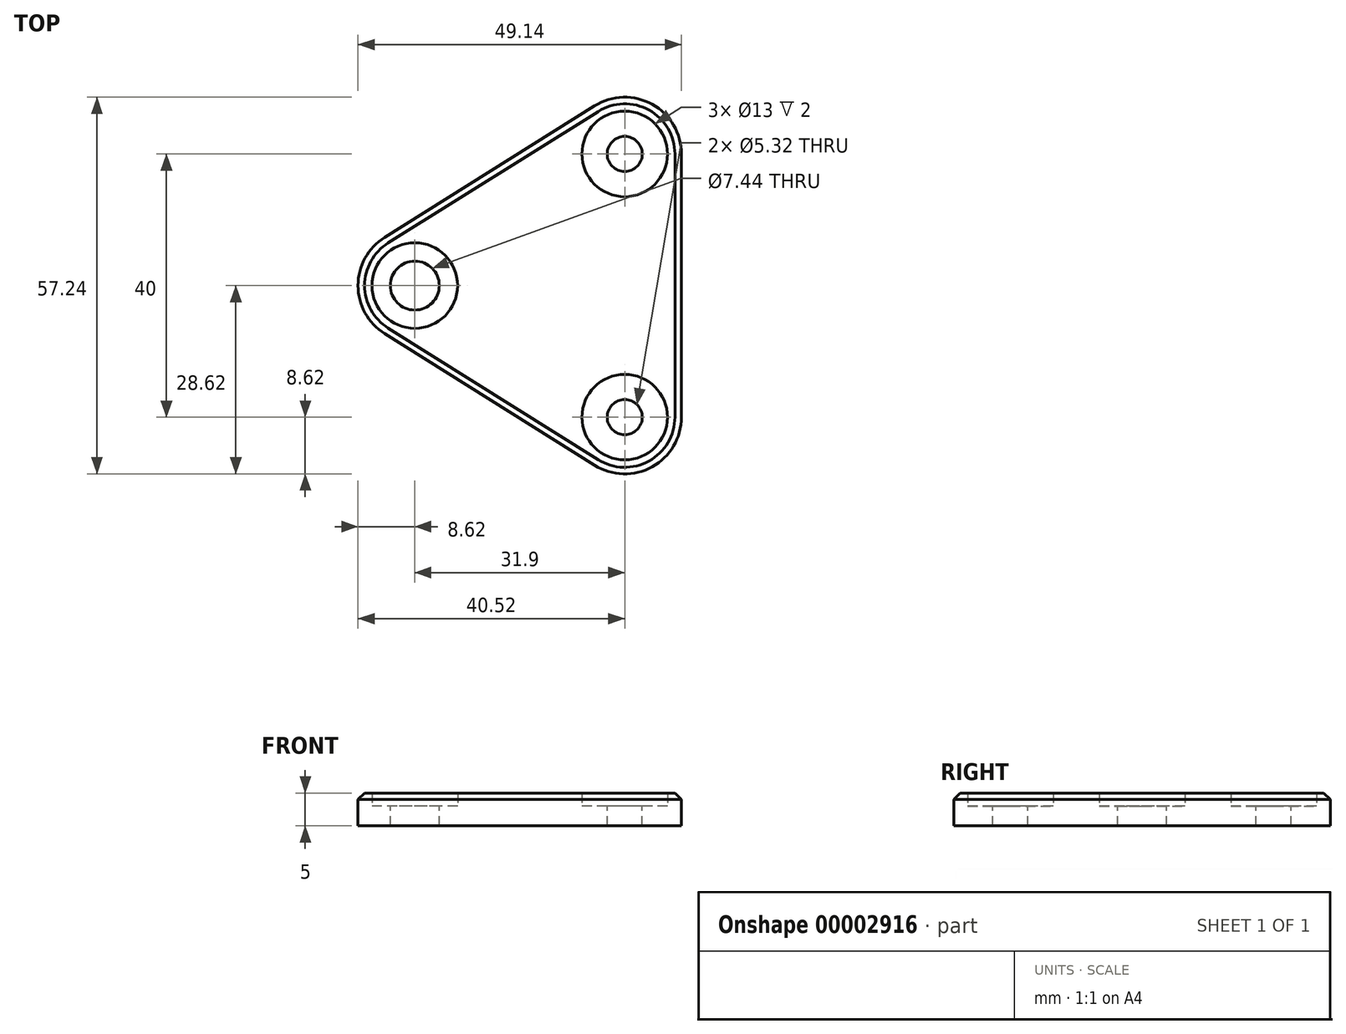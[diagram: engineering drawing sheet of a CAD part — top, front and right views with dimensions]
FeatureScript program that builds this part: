
annotation { "Feature Type Name" : "Feature", "Feature Type Description" : "" }
export const myFeature = defineFeature(function(context is Context, id is Id, definition is map)
    precondition{}
    {
        {
            var Q0;
            Q0=qCreatedBy(makeId("Top.planeOp"),FACE);
            var sketch = newSketch(context, id + "F0", { "sketchPlane" : qUnion([Q0])});
            skCircle(sketch, "E0", {"center": v(15.95, 20) * mm, "radius": 2.66 * mm});
            skCircle(sketch, "E1", {"center": v(15.95, -20) * mm, "radius": 2.66 * mm});
            skCircle(sketch, "E2", {"center": v(-15.95, 0) * mm, "radius": 3.72 * mm});
            skLineSegment(sketch, "E3", {"start": v(15.95, 20) * mm, "end": v(15.95, -20) * mm, "construction": true});
            skLineSegment(sketch, "E4", {"start": v(-15.95, 0) * mm, "end": v(15.95, 0) * mm, "construction": true});
            skLineSegment(sketch, "E5", {"start": v(-20.53, 7.3) * mm, "end": v(11.37, 27.3) * mm});
            skLineSegment(sketch, "E6", {"start": v(-20.53, -7.3) * mm, "end": v(11.37, -27.3) * mm});
            skLineSegment(sketch, "E7", {"start": v(24.57, -20) * mm, "end": v(24.57, 20) * mm});
            skArc(sketch, "E8", {"start": v(-20.53, 7.3) * mm, "mid": v(-24.57, 0) * mm, "end": v(-20.53, -7.3) * mm});
            skArc(sketch, "E9", {"start": v(11.37, 27.3) * mm, "mid": v(20.12, 27.54) * mm, "end": v(24.57, 20) * mm});
            skArc(sketch, "E10", {"start": v(11.37, -27.3) * mm, "mid": v(20.12, -27.54) * mm, "end": v(24.57, -20) * mm});
            skCircle(sketch, "E11", {"center": v(-15.95, 0) * mm, "radius": 6.5 * mm});
            skCircle(sketch, "E12", {"center": v(15.95, 20) * mm, "radius": 6.5 * mm});
            skCircle(sketch, "E13", {"center": v(15.95, -20) * mm, "radius": 6.5 * mm});
            skSolve(sketch);
        }
        {
            var Q0;
            Q0=makeQuery(id+"F0.imprint","IMPRINT",FACE,{"disambiguationData":[TD([[makeQuery(id+"F0.imprint","IMPRINT",EDGE,{"derivedFrom":sQuery(id+"F0.wireOp",EDGE,"E0")}),-1.0]])]});
            var Q1;
            Q1=makeQuery(id+"F0.imprint","IMPRINT",FACE,{"disambiguationData":[TD([[makeQuery(id+"F0.imprint","IMPRINT",EDGE,{"derivedFrom":sQuery(id+"F0.wireOp",EDGE,"E5")}),-1.0]])]});
            var Q2;
            Q2=makeQuery(id+"F0.imprint","IMPRINT",FACE,{"disambiguationData":[TD([[makeQuery(id+"F0.imprint","IMPRINT",EDGE,{"derivedFrom":sQuery(id+"F0.wireOp",EDGE,"E2")}),-1.0]])]});
            var Q3;
            Q3=makeQuery(id+"F0.imprint","IMPRINT",FACE,{"disambiguationData":[TD([[makeQuery(id+"F0.imprint","IMPRINT",EDGE,{"derivedFrom":sQuery(id+"F0.wireOp",EDGE,"E1")}),-1.0]])]});
            extrude(context, id + "F1", {"entities" : qUnion([Q0, Q1, Q2, Q3]), "oppositeDirection" : true, "depth" : 3 * mm});
        }
        {
            var Q0;
            Q0=makeQuery(id+"F0.imprint","IMPRINT",FACE,{"disambiguationData":[TD([[makeQuery(id+"F0.imprint","IMPRINT",EDGE,{"derivedFrom":sQuery(id+"F0.wireOp",EDGE,"E5")}),-1.0]])]});
            extrude(context, id + "F2", {"entities" : qUnion([Q0]), "operationType" : NewBodyOperationType.ADD, "depth" : 2 * mm});
        }
        {
            var Q0;
            Q0=makeQuery(id+"F2.opExtrude","CAP_EDGE",EDGE,{"disambiguationData":[OSD([sQuery(id+"F0.wireOp",EDGE,"E6")])],"isStart":false});
            chamfer(context, id + "F3", {"entities" : qUnion([Q0]), "width" : 1 * mm, "tangentPropagation" : true});
        }
    });
